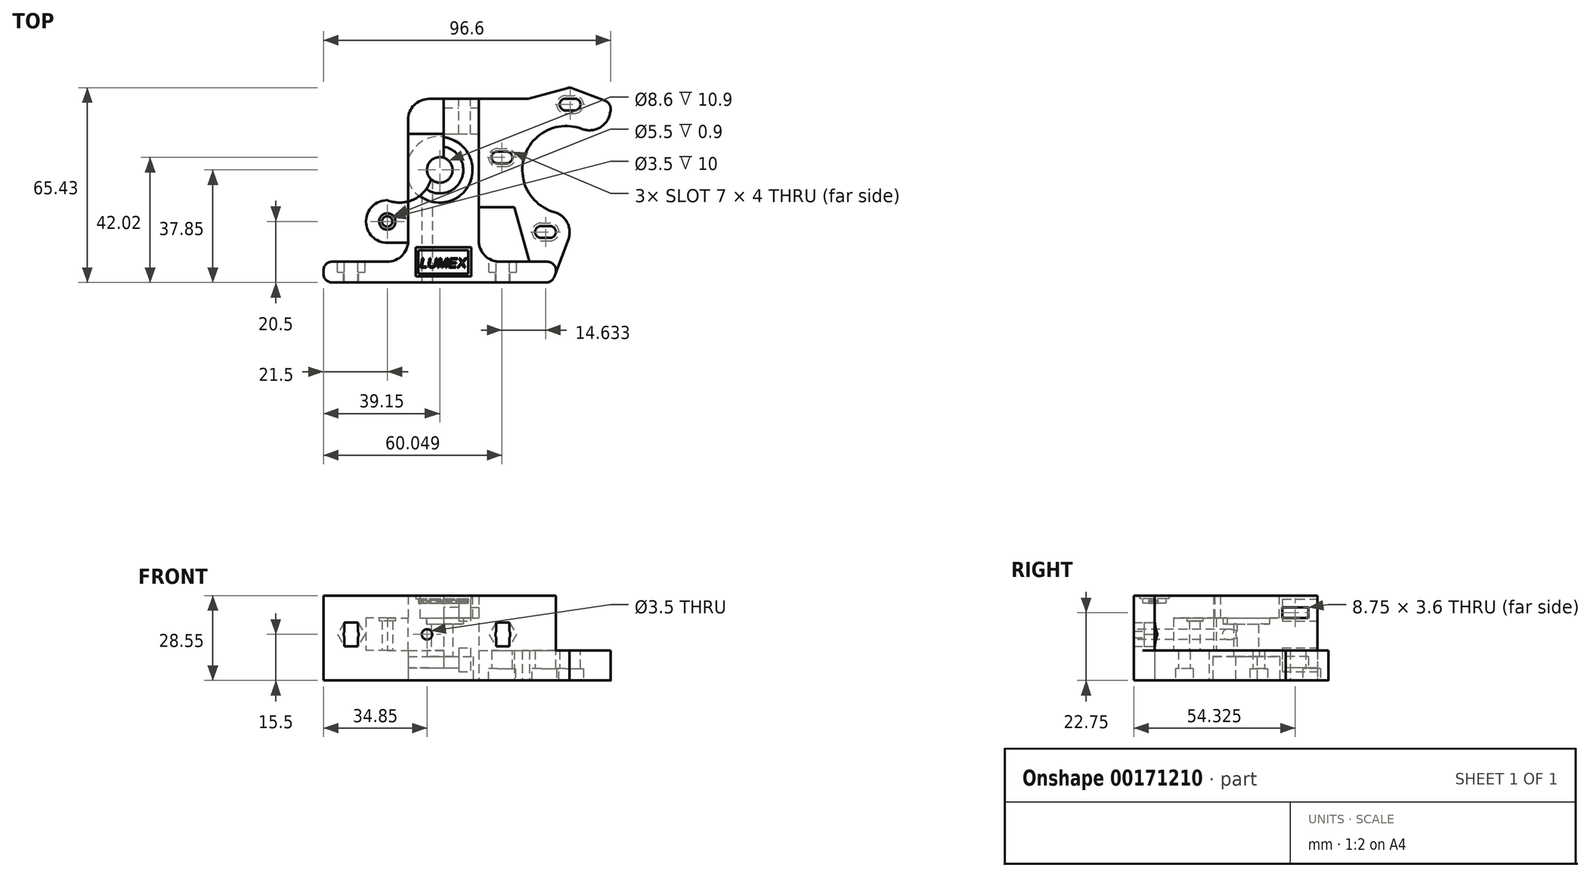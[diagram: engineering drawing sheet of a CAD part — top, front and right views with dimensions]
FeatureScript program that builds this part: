
annotation { "Feature Type Name" : "Feature", "Feature Type Description" : "" }
export const myFeature = defineFeature(function(context is Context, id is Id, definition is map)
    precondition{}
    {
        {
            var Q0;
            Q0=qCreatedBy(makeId("Top.planeOp"),FACE);
            var sketch = newSketch(context, id + "F0", { "sketchPlane" : qUnion([Q0])});
            skCircle(sketch, "E0", {"center": v(0, 0) * mm, "radius": 11.25 * mm});
            skCircle(sketch, "E1", {"center": v(42.5, 0) * mm, "radius": 14.75 * mm});
            skLineSegment(sketch, "E2", {"start": v(-10.65, 23.85) * mm, "end": v(-10.65, -30.85) * mm});
            skLineSegment(sketch, "E3", {"start": v(-10.65, -30.85) * mm, "end": v(-39.15, -30.85) * mm});
            skLineSegment(sketch, "E4", {"start": v(-39.15, -30.85) * mm, "end": v(-39.15, -37.85) * mm});
            skLineSegment(sketch, "E5", {"start": v(-39.15, -37.85) * mm, "end": v(37.75, -37.85) * mm});
            skLineSegment(sketch, "E6", {"start": v(-10.65, 23.85) * mm, "end": v(29.35, 23.85) * mm});
            skLineSegment(sketch, "E7", {"start": v(37.75, -37.85) * mm, "end": v(46.67, -14.15) * mm});
            skLineSegment(sketch, "E8", {"start": v(29.35, 23.85) * mm, "end": v(43.84, 27.73) * mm});
            skLineSegment(sketch, "E9", {"start": v(43.84, 27.73) * mm, "end": v(57.85, 22.35) * mm});
            skLineSegment(sketch, "E10", {"start": v(57.85, 22.35) * mm, "end": v(55.15, 7.6) * mm});
            skLineSegment(sketch, "E11", {"start": v(-10.65, -30.85) * mm, "end": v(40.38, -30.85) * mm});
            skLineSegment(sketch, "E12", {"start": v(13.1, 23.85) * mm, "end": v(13.1, -30.85) * mm});
            skLineSegment(sketch, "E13", {"start": v(13.1, -12.56) * mm, "end": v(25.1, -12.56) * mm});
            skLineSegment(sketch, "E14.bottom", {"start": v(40.3, 23.96) * mm, "end": v(47.3, 23.96) * mm});
            skLineSegment(sketch, "E14.top", {"start": v(40.3, 19.96) * mm, "end": v(47.3, 19.96) * mm});
            skLineSegment(sketch, "E14.left", {"start": v(40.3, 23.96) * mm, "end": v(40.3, 19.96) * mm});
            skLineSegment(sketch, "E14.right", {"start": v(47.3, 23.96) * mm, "end": v(47.3, 19.96) * mm});
            skPoint(sketch, "E14.middle", {"position": v(43.8, 21.96) * mm});
            skLineSegment(sketch, "E15.bottom", {"start": v(17.4, 6.17) * mm, "end": v(24.4, 6.17) * mm});
            skLineSegment(sketch, "E15.top", {"start": v(17.4, 2.17) * mm, "end": v(24.4, 2.17) * mm});
            skLineSegment(sketch, "E15.left", {"start": v(17.4, 6.17) * mm, "end": v(17.4, 2.17) * mm});
            skLineSegment(sketch, "E15.right", {"start": v(24.4, 6.17) * mm, "end": v(24.4, 2.17) * mm});
            skPoint(sketch, "E15.middle", {"position": v(20.9, 4.17) * mm});
            skLineSegment(sketch, "E16.bottom", {"start": v(32.03, -18.87) * mm, "end": v(39.03, -18.87) * mm});
            skLineSegment(sketch, "E16.top", {"start": v(32.03, -22.87) * mm, "end": v(39.03, -22.87) * mm});
            skLineSegment(sketch, "E16.left", {"start": v(32.03, -18.87) * mm, "end": v(32.03, -22.87) * mm});
            skLineSegment(sketch, "E16.right", {"start": v(39.03, -18.87) * mm, "end": v(39.03, -22.87) * mm});
            skPoint(sketch, "E16.middle", {"position": v(35.53, -20.87) * mm});
            skLineSegment(sketch, "E17.bottom", {"start": v(16.4, 7.17) * mm, "end": v(25.4, 7.17) * mm});
            skLineSegment(sketch, "E17.top", {"start": v(16.4, 1.17) * mm, "end": v(25.4, 1.17) * mm});
            skLineSegment(sketch, "E17.left", {"start": v(16.4, 7.17) * mm, "end": v(16.4, 1.17) * mm});
            skLineSegment(sketch, "E17.right", {"start": v(25.4, 7.17) * mm, "end": v(25.4, 1.17) * mm});
            skLineSegment(sketch, "E18.bottom", {"start": v(31.03, -17.87) * mm, "end": v(40.03, -17.87) * mm});
            skLineSegment(sketch, "E18.top", {"start": v(31.03, -23.87) * mm, "end": v(40.03, -23.87) * mm});
            skLineSegment(sketch, "E18.left", {"start": v(31.03, -17.87) * mm, "end": v(31.03, -23.87) * mm});
            skLineSegment(sketch, "E18.right", {"start": v(40.03, -17.87) * mm, "end": v(40.03, -23.87) * mm});
            skLineSegment(sketch, "E19.bottom", {"start": v(39.3, 24.96) * mm, "end": v(48.3, 24.96) * mm});
            skLineSegment(sketch, "E19.top", {"start": v(39.3, 18.96) * mm, "end": v(48.3, 18.96) * mm});
            skLineSegment(sketch, "E19.left", {"start": v(39.3, 24.96) * mm, "end": v(39.3, 18.96) * mm});
            skLineSegment(sketch, "E19.right", {"start": v(48.3, 24.96) * mm, "end": v(48.3, 18.96) * mm});
            skLineSegment(sketch, "E20", {"start": v(25.1, -12.56) * mm, "end": v(30.1, -30.85) * mm});
            skLineSegment(sketch, "E21", {"start": v(-10.65, 12.1) * mm, "end": v(1.35, 12.1) * mm});
            skLineSegment(sketch, "E22", {"start": v(1.35, 12.1) * mm, "end": v(1.35, 23.85) * mm});
            skLineSegment(sketch, "E23", {"start": v(1.35, 20.85) * mm, "end": v(6.35, 20.85) * mm});
            skLineSegment(sketch, "E24", {"start": v(6.35, 20.85) * mm, "end": v(6.35, 23.85) * mm});
            skLineSegment(sketch, "E25", {"start": v(1.35, 12.1) * mm, "end": v(10.35, 12.1) * mm});
            skLineSegment(sketch, "E26", {"start": v(10.35, 12.1) * mm, "end": v(10.35, 23.85) * mm});
            skLineSegment(sketch, "E27", {"start": v(6.35, 20.85) * mm, "end": v(6.35, 12.1) * mm});
            skCircle(sketch, "E28", {"center": v(0, 0) * mm, "radius": 4.3 * mm});
            skSolve(sketch);
        }
        {
            var Q0;
            {var subQ11=sQuery(id+"F0.wireOp",EDGE,"E8");Q0=makeQuery(id+"F0.imprint","IMPRINT",FACE,{"disambiguationData":[TD([[makeQuery(id+"F0.imprint","IMPRINT",EDGE,{"derivedFrom":subQ11}),-1.0]])]});}
            var Q1;
            {var subQ3=sQuery(id+"F0.wireOp",EDGE,"E21");Q1=makeQuery(id+"F0.imprint","IMPRINT",FACE,{"disambiguationData":[TD([[makeQuery(id+"F0.imprint","IMPRINT",EDGE,{"derivedFrom":subQ3}),-1.0]])]});}
            var Q2;
            {var subQ6=sQuery(id+"F0.wireOp",EDGE,"E3");Q2=makeQuery(id+"F0.imprint","IMPRINT",FACE,{"disambiguationData":[TD([[makeQuery(id+"F0.imprint","IMPRINT",EDGE,{"derivedFrom":subQ6}),1.0]])]});}
            var Q3;
            {var subQ4=sQuery(id+"F0.wireOp",EDGE,"E23");Q3=makeQuery(id+"F0.imprint","IMPRINT",FACE,{"disambiguationData":[TD([[makeQuery(id+"F0.imprint","IMPRINT",EDGE,{"derivedFrom":subQ4}),1.0]])]});}
            extrude(context, id + "F1", {"entities" : qUnion([Q0, Q1, Q2, Q3]), "depth" : 10.05 * mm});
        }
        {
            var Q0;
            Q0=makeQuery(id+"F0.imprint","IMPRINT",FACE,{"disambiguationData":[TD([[makeQuery(id+"F0.imprint","IMPRINT",EDGE,{"derivedFrom":sQuery(id+"F0.wireOp",EDGE,"E15.bottom")}),1.0]])]});
            var Q1;
            Q1=makeQuery(id+"F0.imprint","IMPRINT",FACE,{"disambiguationData":[TD([[makeQuery(id+"F0.imprint","IMPRINT",EDGE,{"derivedFrom":sQuery(id+"F0.wireOp",EDGE,"E14.bottom")}),1.0]])]});
            var Q2;
            Q2=makeQuery(id+"F0.imprint","IMPRINT",FACE,{"disambiguationData":[TD([[makeQuery(id+"F0.imprint","IMPRINT",EDGE,{"derivedFrom":sQuery(id+"F0.wireOp",EDGE,"E16.bottom")}),1.0]])]});
            extrude(context, id + "F2", {"entities" : qUnion([Q0, Q1, Q2]), "operationType" : NewBodyOperationType.ADD, "depth" : 10.05 * mm, "hasSecondDirection" : true, "secondDirectionOppositeDirection" : false, "secondDirectionDepth" : 4 * mm});
        }
        {
            var Q0;
            {var subQ3=sQuery(id+"F0.wireOp",EDGE,"E23");Q0=makeQuery(id+"F0.imprint","IMPRINT",FACE,{"disambiguationData":[TD([[makeQuery(id+"F0.imprint","IMPRINT",EDGE,{"derivedFrom":subQ3}),-1.0]])]});}
            var Q1;
            {var subQ1=sQuery(id+"F0.wireOp",EDGE,"E21");Q1=makeQuery(id+"F0.imprint","IMPRINT",FACE,{"disambiguationData":[TD([[makeQuery(id+"F0.imprint","IMPRINT",EDGE,{"derivedFrom":subQ1}),1.0]])]});}
            extrude(context, id + "F3", {"entities" : qUnion([Q0, Q1]), "operationType" : NewBodyOperationType.ADD, "depth" : 4.25 * mm});
        }
        {
            var Q0;
            {var subQ0=sQuery(id+"F0.wireOp",EDGE,"E24");Q0=makeQuery(id+"F0.imprint","IMPRINT",FACE,{"disambiguationData":[TD([[makeQuery(id+"F0.imprint","IMPRINT",EDGE,{"derivedFrom":subQ0}),-1.0]])]});}
            extrude(context, id + "F4", {"entities" : qUnion([Q0]), "operationType" : NewBodyOperationType.ADD, "depth" : 3 * mm});
        }
        {
            var Q0;
            Q0=makeQuery(id+"F0.imprint","IMPRINT",FACE,{"disambiguationData":[TD([[makeQuery(id+"F0.imprint","IMPRINT",EDGE,{"derivedFrom":sQuery(id+"F0.wireOp",EDGE,"E28")}),-1.0]])]});
            var Q1;
            {var subQ3=sQuery(id+"F0.wireOp",EDGE,"E23");Q1=makeQuery(id+"F0.imprint","IMPRINT",FACE,{"disambiguationData":[TD([[makeQuery(id+"F0.imprint","IMPRINT",EDGE,{"derivedFrom":subQ3}),-1.0]])]});}
            extrude(context, id + "F5", {"entities" : qUnion([Q0, Q1]), "operationType" : NewBodyOperationType.ADD, "depth" : 10.05 * mm, "hasSecondDirection" : true, "secondDirectionOppositeDirection" : false, "secondDirectionDepth" : 8.05 * mm});
        }
        {
            var Q0;
            {var subQ0=sQuery(id+"F0.wireOp",EDGE,"E25");var subQ1=sQuery(id+"F0.wireOp",EDGE,"E23");var subQ2=sQuery(id+"F0.wireOp",EDGE,"E22");var subQ3=sQuery(id+"F0.wireOp",EDGE,"E2");var subQ4=sQuery(id+"F0.wireOp",EDGE,"E0");var subQ5=sQuery(id+"F0.wireOp",EDGE,"E18.right");var subQ6=sQuery(id+"F0.wireOp",EDGE,"E18.left");var subQ7=sQuery(id+"F0.wireOp",EDGE,"E18.top");var subQ8=sQuery(id+"F0.wireOp",EDGE,"E18.bottom");var subQ9=sQuery(id+"F0.wireOp",EDGE,"E17.right");var subQ10=sQuery(id+"F0.wireOp",EDGE,"E17.left");var subQ11=sQuery(id+"F0.wireOp",EDGE,"E17.top");var subQ12=sQuery(id+"F0.wireOp",EDGE,"E17.bottom");var subQ13=sQuery(id+"F0.wireOp",EDGE,"E19.right");var subQ14=sQuery(id+"F0.wireOp",EDGE,"E19.left");var subQ15=sQuery(id+"F0.wireOp",EDGE,"E19.top");var subQ16=sQuery(id+"F0.wireOp",EDGE,"E19.bottom");var subQ17=sQuery(id+"F0.wireOp",EDGE,"E6");Q0=makeQuery(id+"F5.boolean.opBoolean","MERGE",FACE,{"derivedFrom":[makeQuery(id+"F1.opExtrude","CAP_FACE",FACE,{"disambiguationData":[OSD([subQ17,subQ2,subQ1,sQuery(id+"F0.wireOp",EDGE,"E24")])],"isStart":false}),makeQuery(id+"F2.boolean.opBoolean","MERGE",FACE,{"derivedFrom":[makeQuery(id+"F1.opExtrude","CAP_FACE",FACE,{"disambiguationData":[OSD([subQ4,sQuery(id+"F0.wireOp",EDGE,"E1"),subQ3,sQuery(id+"F0.wireOp",EDGE,"E3"),sQuery(id+"F0.wireOp",EDGE,"E4"),sQuery(id+"F0.wireOp",EDGE,"E5"),subQ17,sQuery(id+"F0.wireOp",EDGE,"E7"),sQuery(id+"F0.wireOp",EDGE,"E8"),sQuery(id+"F0.wireOp",EDGE,"E9"),sQuery(id+"F0.wireOp",EDGE,"E10"),sQuery(id+"F0.wireOp",EDGE,"E11"),sQuery(id+"F0.wireOp",EDGE,"E12"),sQuery(id+"F0.wireOp",EDGE,"E13"),subQ12,subQ11,subQ10,subQ9,subQ8,subQ7,subQ6,subQ5,subQ16,subQ15,subQ14,subQ13,sQuery(id+"F0.wireOp",EDGE,"E20"),sQuery(id+"F0.wireOp",EDGE,"E21"),subQ0,sQuery(id+"F0.wireOp",EDGE,"E26")])],"isStart":false}),makeQuery(id+"F2.opExtrude","CAP_FACE",FACE,{"disambiguationData":[OSD([sQuery(id+"F0.wireOp",EDGE,"E14.bottom"),sQuery(id+"F0.wireOp",EDGE,"E14.top"),sQuery(id+"F0.wireOp",EDGE,"E14.left"),sQuery(id+"F0.wireOp",EDGE,"E14.right"),subQ16,subQ15,subQ14,subQ13])],"isStart":false}),makeQuery(id+"F2.opExtrude","CAP_FACE",FACE,{"disambiguationData":[OSD([sQuery(id+"F0.wireOp",EDGE,"E15.bottom"),sQuery(id+"F0.wireOp",EDGE,"E15.top"),sQuery(id+"F0.wireOp",EDGE,"E15.left"),sQuery(id+"F0.wireOp",EDGE,"E15.right"),subQ12,subQ11,subQ10,subQ9])],"isStart":false}),makeQuery(id+"F2.opExtrude","CAP_FACE",FACE,{"disambiguationData":[OSD([sQuery(id+"F0.wireOp",EDGE,"E16.bottom"),sQuery(id+"F0.wireOp",EDGE,"E16.top"),sQuery(id+"F0.wireOp",EDGE,"E16.left"),sQuery(id+"F0.wireOp",EDGE,"E16.right"),subQ8,subQ7,subQ6,subQ5])],"isStart":false})]}),makeQuery(id+"F5.opExtrude","CAP_FACE",FACE,{"disambiguationData":[OSD([subQ4,subQ3,sQuery(id+"F0.wireOp",EDGE,"E28")])],"isStart":false}),makeQuery(id+"F5.opExtrude","CAP_FACE",FACE,{"disambiguationData":[OSD([subQ2,subQ1,subQ0,sQuery(id+"F0.wireOp",EDGE,"E27")])],"isStart":false})]});}
            var sketch = newSketch(context, id + "F6", { "sketchPlane" : qUnion([Q0])});
            skLineSegment(sketch, "E29", {"start": v(13.1, -30.85) * mm, "end": v(13.1, 23.85) * mm});
            skLineSegment(sketch, "E30", {"start": v(13.1, -30.85) * mm, "end": v(13.1, -37.85) * mm});
            skLineSegment(sketch, "E31", {"start": v(-10.65, -30.85) * mm, "end": v(-10.65, -37.85) * mm});
            skLineSegment(sketch, "E32", {"start": v(-10.65, -30.85) * mm, "end": v(-10.65, 23.85) * mm});
            skLineSegment(sketch, "E33", {"start": v(-10.65, 23.85) * mm, "end": v(13.1, 23.85) * mm});
            skCircle(sketch, "E34", {"center": v(0, 0) * mm, "radius": 4.3 * mm});
            skCircle(sketch, "E35", {"center": v(0, 0) * mm, "radius": 7.9 * mm});
            skCircle(sketch, "E36", {"center": v(0, 0) * mm, "radius": 11 * mm});
            skLineSegment(sketch, "E37", {"start": v(1.35, 23.85) * mm, "end": v(1.35, 4.08) * mm});
            skLineSegment(sketch, "E38", {"start": v(13.1, -30.85) * mm, "end": v(40.38, -30.85) * mm});
            skLineSegment(sketch, "E39", {"start": v(40.38, -30.85) * mm, "end": v(37.75, -37.85) * mm});
            skLineSegment(sketch, "E40", {"start": v(37.75, -37.85) * mm, "end": v(13.1, -37.85) * mm});
            skLineSegment(sketch, "E41", {"start": v(-10.65, -30.85) * mm, "end": v(-39.15, -30.85) * mm});
            skLineSegment(sketch, "E42", {"start": v(-39.15, -30.85) * mm, "end": v(-39.15, -37.85) * mm});
            skLineSegment(sketch, "E43", {"start": v(-39.15, -37.85) * mm, "end": v(-10.65, -37.85) * mm});
            skCircle(sketch, "E44", {"center": v(-13.5, 0) * mm, "radius": 11 * mm});
            skCircle(sketch, "E45", {"center": v(-17.65, -17.35) * mm, "radius": 1.75 * mm});
            skArc(sketch, "E46", {"start": v(-17.65, -10.19) * mm, "mid": v(-24.81, -17.35) * mm, "end": v(-17.65, -24.51) * mm});
            skLineSegment(sketch, "E47", {"start": v(-17.65, -24.51) * mm, "end": v(-10.65, -24.51) * mm});
            skCircle(sketch, "E48", {"center": v(-17.65, -17.35) * mm, "radius": 2.75 * mm});
            skLineSegment(sketch, "E49", {"start": v(6.35, 23.85) * mm, "end": v(6.35, 12.1) * mm});
            skLineSegment(sketch, "E50", {"start": v(6.35, 12.1) * mm, "end": v(10.35, 12.1) * mm});
            skLineSegment(sketch, "E51", {"start": v(10.35, 12.1) * mm, "end": v(10.35, 23.85) * mm});
            skLineSegment(sketch, "E52", {"start": v(10.35, 23.85) * mm, "end": v(6.35, 23.85) * mm});
            skLineSegment(sketch, "E53", {"start": v(35.02, -30.85) * mm, "end": v(35.02, -37.85) * mm});
            skSolve(sketch);
        }
        {
            var Q0;
            {var subQ0=sQuery(id+"F6.wireOp",EDGE,"E37");var subQ1=sQuery(id+"F6.wireOp",EDGE,"E35");var subQ2=makeQuery(id+"F6.imprint","INTERSECT",VERTEX,{"derivedFrom":[subQ1,subQ0]});Q0=makeQuery(id+"F6.imprint","IMPRINT",FACE,{"disambiguationData":[TD([[makeQuery(id+"F6.imprint","IMPRINT",EDGE,{"disambiguationData":[TD([[subQ2,1.0]])],"derivedFrom":subQ1}),-1.0]])]});}
            var Q1;
            {var subQ1=sQuery(id+"F6.wireOp",EDGE,"E46");Q1=makeQuery(id+"F6.imprint","IMPRINT",FACE,{"disambiguationData":[TD([[makeQuery(id+"F6.imprint","IMPRINT",EDGE,{"derivedFrom":subQ1}),1.0]])]});}
            var Q2;
            {var subQ9=sQuery(id+"F6.wireOp",EDGE,"E30");Q2=makeQuery(id+"F6.imprint","IMPRINT",FACE,{"disambiguationData":[TD([[makeQuery(id+"F6.imprint","IMPRINT",EDGE,{"derivedFrom":subQ9}),-1.0]])]});}
            var Q3;
            {var subQ0=sQuery(id+"F6.wireOp",EDGE,"E39");Q3=makeQuery(id+"F6.imprint","IMPRINT",FACE,{"disambiguationData":[TD([[makeQuery(id+"F6.imprint","IMPRINT",EDGE,{"derivedFrom":subQ0}),1.0]])]});}
            extrude(context, id + "F7", {"entities" : qUnion([Q0, Q1, Q2, Q3]), "operationType" : NewBodyOperationType.ADD, "depth" : 10.9 * mm});
        }
        {
            var Q0;
            {var subQ0=sQuery(id+"F6.wireOp",EDGE,"E37");var subQ1=sQuery(id+"F6.wireOp",EDGE,"E34");var subQ2=makeQuery(id+"F6.imprint","INTERSECT",VERTEX,{"derivedFrom":[subQ1,subQ0]});Q0=makeQuery(id+"F6.imprint","IMPRINT",FACE,{"disambiguationData":[TD([[makeQuery(id+"F6.imprint","IMPRINT",EDGE,{"disambiguationData":[TD([[subQ2,1.0]])],"derivedFrom":subQ1}),-1.0]])]});}
            extrude(context, id + "F8", {"entities" : qUnion([Q0]), "operationType" : NewBodyOperationType.ADD, "depth" : 8.9 * mm});
        }
        {
            var Q0;
            Q0=makeQuery(id+"F6.imprint","IMPRINT",FACE,{"disambiguationData":[TD([[makeQuery(id+"F6.imprint","IMPRINT",EDGE,{"derivedFrom":sQuery(id+"F6.wireOp",EDGE,"E49")}),-1.0]])]});
            extrude(context, id + "F9", {"entities" : qUnion([Q0]), "operationType" : NewBodyOperationType.ADD, "depth" : 10 * mm, "hasSecondDirection" : true, "secondDirectionOppositeDirection" : false, "secondDirectionDepth" : .9 * mm});
        }
        {
            var Q0;
            Q0=makeQuery(id+"F6.imprint","IMPRINT",FACE,{"disambiguationData":[TD([[makeQuery(id+"F6.imprint","IMPRINT",EDGE,{"derivedFrom":sQuery(id+"F6.wireOp",EDGE,"E31")}),-1.0]])]});
            var Q1;
            {var subQ3=sQuery(id+"F6.wireOp",EDGE,"E30");Q1=makeQuery(id+"F6.imprint","IMPRINT",FACE,{"disambiguationData":[TD([[makeQuery(id+"F6.imprint","IMPRINT",EDGE,{"derivedFrom":subQ3}),1.0]])]});}
            extrude(context, id + "F10", {"entities" : qUnion([Q0, Q1]), "operationType" : NewBodyOperationType.ADD, "depth" : 1.45 * mm});
        }
        {
            var Q0;
            Q0=makeQuery(id+"F6.imprint","IMPRINT",FACE,{"disambiguationData":[TD([[makeQuery(id+"F6.imprint","IMPRINT",EDGE,{"derivedFrom":sQuery(id+"F6.wireOp",EDGE,"E31")}),-1.0]])]});
            var Q1;
            {var subQ3=sQuery(id+"F6.wireOp",EDGE,"E30");Q1=makeQuery(id+"F6.imprint","IMPRINT",FACE,{"disambiguationData":[TD([[makeQuery(id+"F6.imprint","IMPRINT",EDGE,{"derivedFrom":subQ3}),1.0]])]});}
            extrude(context, id + "F11", {"entities" : qUnion([Q0, Q1]), "operationType" : NewBodyOperationType.ADD, "depth" : 10.9 * mm, "hasSecondDirection" : true, "secondDirectionOppositeDirection" : false, "secondDirectionDepth" : 9.45 * mm});
        }
        {
            var Q0;
            Q0=makeQuery(id+"F11.opExtrude","SWEPT_FACE",FACE,{"disambiguationData":[OSD([sQuery(id+"F6.wireOp",EDGE,"E38")])]});
            var sketch = newSketch(context, id + "F12", { "sketchPlane" : qUnion([Q0])});
            skLineSegment(sketch, "E54", {"start": v(-35.02, 19.5) * mm, "end": v(-13.1, 19.5) * mm});
            skLineSegment(sketch, "E55", {"start": v(-35.02, 19.5) * mm, "end": v(-35.02, 11.5) * mm});
            skLineSegment(sketch, "E56", {"start": v(-13.1, 19.5) * mm, "end": v(-13.1, 11.5) * mm});
            skLineSegment(sketch, "E57", {"start": v(-35.02, 11.5) * mm, "end": v(-13.1, 11.5) * mm});
            skLineSegment(sketch, "E58.bottom", {"start": v(-23.45, 19.5) * mm, "end": v(-18.95, 19.5) * mm});
            skLineSegment(sketch, "E58.top", {"start": v(-23.45, 11.5) * mm, "end": v(-18.95, 11.5) * mm});
            skLineSegment(sketch, "E58.left", {"start": v(-23.45, 19.5) * mm, "end": v(-23.45, 11.5) * mm});
            skLineSegment(sketch, "E58.right", {"start": v(-18.95, 19.5) * mm, "end": v(-18.95, 11.5) * mm});
            skLineSegment(sketch, "E59", {"start": v(-23.45, 19.5) * mm, "end": v(-25.82, 15.5) * mm});
            skLineSegment(sketch, "E60", {"start": v(-25.82, 15.5) * mm, "end": v(-23.45, 11.5) * mm});
            skLineSegment(sketch, "E61", {"start": v(-18.95, 19.5) * mm, "end": v(-16.57, 15.5) * mm});
            skLineSegment(sketch, "E62", {"start": v(-16.57, 15.5) * mm, "end": v(-18.95, 11.5) * mm});
            skLineSegment(sketch, "E63", {"start": v(-25.82, 15.5) * mm, "end": v(-23.45, 15.5) * mm});
            skLineSegment(sketch, "E64", {"start": v(-16.57, 15.5) * mm, "end": v(-18.95, 15.5) * mm});
            skCircle(sketch, "E65", {"center": v(-21.2, 15.5) * mm, "radius": 2.5 * mm});
            skLineSegment(sketch, "E66", {"start": v(-13.1, 11.5) * mm, "end": v(39.15, 11.5) * mm});
            skLineSegment(sketch, "E67", {"start": v(-13.1, 19.5) * mm, "end": v(39.15, 19.5) * mm});
            skLineSegment(sketch, "E68", {"start": v(39.15, 19.5) * mm, "end": v(39.15, 11.5) * mm});
            skCircle(sketch, "E69", {"center": v(29.8, 15.5) * mm, "radius": 2.5 * mm});
            skLineSegment(sketch, "E70", {"start": v(32.05, 19.5) * mm, "end": v(32.05, 11.5) * mm});
            skLineSegment(sketch, "E71", {"start": v(27.55, 19.5) * mm, "end": v(27.55, 11.5) * mm});
            skLineSegment(sketch, "E72", {"start": v(27.55, 19.5) * mm, "end": v(25.17, 15.5) * mm});
            skLineSegment(sketch, "E73", {"start": v(25.17, 15.5) * mm, "end": v(27.55, 11.5) * mm});
            skLineSegment(sketch, "E74", {"start": v(32.05, 19.5) * mm, "end": v(34.42, 15.5) * mm});
            skLineSegment(sketch, "E75", {"start": v(34.42, 15.5) * mm, "end": v(32.05, 11.5) * mm});
            skLineSegment(sketch, "E76", {"start": v(34.42, 15.5) * mm, "end": v(32.05, 15.5) * mm});
            skLineSegment(sketch, "E77", {"start": v(25.18, 15.5) * mm, "end": v(27.55, 15.5) * mm});
            skSolve(sketch);
        }
        {
            var Q0;
            {var subQ0=sQuery(id+"F12.wireOp",EDGE,"E59");Q0=makeQuery(id+"F12.imprint","IMPRINT",FACE,{"disambiguationData":[TD([[makeQuery(id+"F12.imprint","IMPRINT",EDGE,{"derivedFrom":subQ0}),1.0]])]});}
            var Q1;
            {var subQ0=sQuery(id+"F12.wireOp",EDGE,"E60");Q1=makeQuery(id+"F12.imprint","IMPRINT",FACE,{"disambiguationData":[TD([[makeQuery(id+"F12.imprint","IMPRINT",EDGE,{"derivedFrom":subQ0}),1.0]])]});}
            var Q2;
            {var subQ0=sQuery(id+"F12.wireOp",EDGE,"E62");Q2=makeQuery(id+"F12.imprint","IMPRINT",FACE,{"disambiguationData":[TD([[makeQuery(id+"F12.imprint","IMPRINT",EDGE,{"derivedFrom":subQ0}),-1.0]])]});}
            var Q3;
            {var subQ0=sQuery(id+"F12.wireOp",EDGE,"E61");Q3=makeQuery(id+"F12.imprint","IMPRINT",FACE,{"disambiguationData":[TD([[makeQuery(id+"F12.imprint","IMPRINT",EDGE,{"derivedFrom":subQ0}),-1.0]])]});}
            var Q4;
            {var subQ0=sQuery(id+"F12.wireOp",EDGE,"E58.bottom");Q4=makeQuery(id+"F12.imprint","IMPRINT",FACE,{"disambiguationData":[TD([[makeQuery(id+"F12.imprint","IMPRINT",EDGE,{"derivedFrom":subQ0}),1.0]])]});}
            var Q5;
            {var subQ5=sQuery(id+"F12.wireOp",EDGE,"E75");Q5=makeQuery(id+"F12.imprint","IMPRINT",FACE,{"disambiguationData":[TD([[makeQuery(id+"F12.imprint","IMPRINT",EDGE,{"derivedFrom":subQ5}),-1.0]])]});}
            var Q6;
            {var subQ3=sQuery(id+"F12.wireOp",EDGE,"E71");var subQ5=sQuery(id+"F12.wireOp",EDGE,"E69");var subQ6=makeQuery(id+"F12.imprint","INTERSECT",VERTEX,{"disambiguationData":[OD(1.0)],"derivedFrom":[subQ5,subQ3]});Q6=makeQuery(id+"F12.imprint","IMPRINT",FACE,{"disambiguationData":[TD([[makeQuery(id+"F12.imprint","IMPRINT",EDGE,{"disambiguationData":[TD([[subQ6,-1.0]])],"derivedFrom":subQ5}),-1.0]])]});}
            var Q7;
            {var subQ5=sQuery(id+"F12.wireOp",EDGE,"E73");Q7=makeQuery(id+"F12.imprint","IMPRINT",FACE,{"disambiguationData":[TD([[makeQuery(id+"F12.imprint","IMPRINT",EDGE,{"derivedFrom":subQ5}),1.0]])]});}
            var Q8;
            {var subQ0=sQuery(id+"F12.wireOp",EDGE,"E70");var subQ5=sQuery(id+"F12.wireOp",EDGE,"E69");var subQ6=makeQuery(id+"F12.imprint","INTERSECT",VERTEX,{"disambiguationData":[OD(0.0)],"derivedFrom":[subQ5,subQ0]});Q8=makeQuery(id+"F12.imprint","IMPRINT",FACE,{"disambiguationData":[TD([[makeQuery(id+"F12.imprint","IMPRINT",EDGE,{"disambiguationData":[TD([[subQ6,-1.0]])],"derivedFrom":subQ5}),-1.0]])]});}
            var Q9;
            {var subQ5=sQuery(id+"F12.wireOp",EDGE,"E72");Q9=makeQuery(id+"F12.imprint","IMPRINT",FACE,{"disambiguationData":[TD([[makeQuery(id+"F12.imprint","IMPRINT",EDGE,{"derivedFrom":subQ5}),1.0]])]});}
            var Q10;
            {var subQ5=sQuery(id+"F12.wireOp",EDGE,"E74");Q10=makeQuery(id+"F12.imprint","IMPRINT",FACE,{"disambiguationData":[TD([[makeQuery(id+"F12.imprint","IMPRINT",EDGE,{"derivedFrom":subQ5}),-1.0]])]});}
            var Q11;
            {var subQ0=sQuery(id+"F12.wireOp",EDGE,"E58.top");Q11=makeQuery(id+"F12.imprint","IMPRINT",FACE,{"disambiguationData":[TD([[makeQuery(id+"F12.imprint","IMPRINT",EDGE,{"derivedFrom":subQ0}),-1.0]])]});}
            extrude(context, id + "F13", {"entities" : qUnion([Q0, Q1, Q2, Q3, Q4, Q5, Q6, Q7, Q8, Q9, Q10, Q11]), "operationType" : NewBodyOperationType.ADD, "oppositeDirection" : true, "depth" : 7 * mm, "hasSecondDirection" : true, "secondDirectionOppositeDirection" : true, "secondDirectionDepth" : 3.5 * mm});
        }
        {
            var Q0;
            {var subQ0=sQuery(id+"F12.wireOp",EDGE,"E56");Q0=makeQuery(id+"F12.imprint","IMPRINT",FACE,{"disambiguationData":[TD([[makeQuery(id+"F12.imprint","IMPRINT",EDGE,{"derivedFrom":subQ0}),-1.0]])]});}
            var Q1;
            {var subQ1=sQuery(id+"F12.wireOp",EDGE,"E68");Q1=makeQuery(id+"F12.imprint","IMPRINT",FACE,{"disambiguationData":[TD([[makeQuery(id+"F12.imprint","IMPRINT",EDGE,{"derivedFrom":subQ1}),-1.0]])]});}
            var Q2;
            {var subQ1=sQuery(id+"F12.wireOp",EDGE,"E56");Q2=makeQuery(id+"F12.imprint","IMPRINT",FACE,{"disambiguationData":[TD([[makeQuery(id+"F12.imprint","IMPRINT",EDGE,{"derivedFrom":subQ1}),1.0]])]});}
            var Q3;
            {var subQ2=sQuery(id+"F12.wireOp",EDGE,"E55");Q3=makeQuery(id+"F12.imprint","IMPRINT",FACE,{"disambiguationData":[TD([[makeQuery(id+"F12.imprint","IMPRINT",EDGE,{"derivedFrom":subQ2}),1.0]])]});}
            extrude(context, id + "F14", {"entities" : qUnion([Q0, Q1, Q2, Q3]), "operationType" : NewBodyOperationType.ADD, "oppositeDirection" : true, "depth" : 7 * mm});
        }
        {
            var Q0;
            {var subQ0=sQuery(id+"F6.wireOp",EDGE,"E31");var subQ1=sQuery(id+"F6.wireOp",EDGE,"E53");var subQ2=sQuery(id+"F6.wireOp",EDGE,"E40");var subQ3=sQuery(id+"F6.wireOp",EDGE,"E38");var subQ4=sQuery(id+"F6.wireOp",EDGE,"E30");Q0=makeQuery(id+"F11.boolean.opBoolean","MERGE",FACE,{"derivedFrom":[makeQuery(id+"F7.opExtrude","CAP_FACE",FACE,{"disambiguationData":[OSD([sQuery(id+"F0.wireOp",EDGE,"E5"),sQuery(id+"F6.wireOp",EDGE,"E29"),subQ4,subQ0,sQuery(id+"F6.wireOp",EDGE,"E32"),sQuery(id+"F6.wireOp",EDGE,"E33"),sQuery(id+"F6.wireOp",EDGE,"E35"),sQuery(id+"F6.wireOp",EDGE,"E37"),sQuery(id+"F6.wireOp",EDGE,"E44"),sQuery(id+"F6.wireOp",EDGE,"E46"),sQuery(id+"F6.wireOp",EDGE,"E47"),sQuery(id+"F6.wireOp",EDGE,"E48"),sQuery(id+"F6.wireOp",EDGE,"E49"),sQuery(id+"F6.wireOp",EDGE,"E50"),sQuery(id+"F6.wireOp",EDGE,"E51")])],"isStart":false}),makeQuery(id+"F7.opExtrude","CAP_FACE",FACE,{"disambiguationData":[OSD([subQ3,sQuery(id+"F6.wireOp",EDGE,"E39"),subQ2,subQ1])],"isStart":false}),makeQuery(id+"F11.opExtrude","CAP_FACE",FACE,{"disambiguationData":[OSD([subQ4,subQ3,subQ2,subQ1])],"isStart":false}),makeQuery(id+"F11.opExtrude","CAP_FACE",FACE,{"disambiguationData":[OSD([subQ0,sQuery(id+"F6.wireOp",EDGE,"E41"),sQuery(id+"F6.wireOp",EDGE,"E42"),sQuery(id+"F6.wireOp",EDGE,"E43")])],"isStart":false})]});}
            var sketch = newSketch(context, id + "F15", { "sketchPlane" : qUnion([Q0])});
            skCircle(sketch, "E78", {"center": v(0, 0) * mm, "radius": 11 * mm});
            skLineSegment(sketch, "E79", {"start": v(1.35, 23.85) * mm, "end": v(1.35, 10.92) * mm});
            skLineSegment(sketch, "E80", {"start": v(1.35, 23.85) * mm, "end": v(6.35, 23.85) * mm});
            skLineSegment(sketch, "E81", {"start": v(6.35, 23.85) * mm, "end": v(6.35, 12.1) * mm});
            skLineSegment(sketch, "E82", {"start": v(6.35, 12.1) * mm, "end": v(10.35, 12.1) * mm});
            skLineSegment(sketch, "E83", {"start": v(10.35, 12.1) * mm, "end": v(10.35, 23.85) * mm});
            skLineSegment(sketch, "E84", {"start": v(10.35, 23.85) * mm, "end": v(13.1, 23.85) * mm});
            skLineSegment(sketch, "E85", {"start": v(13.1, 23.85) * mm, "end": v(13.1, -30.85) * mm});
            skLineSegment(sketch, "E86", {"start": v(13.1, -30.85) * mm, "end": v(40.38, -30.85) * mm});
            skLineSegment(sketch, "E87", {"start": v(40.38, -30.85) * mm, "end": v(37.75, -37.85) * mm});
            skLineSegment(sketch, "E88", {"start": v(37.75, -37.85) * mm, "end": v(-39.15, -37.85) * mm});
            skLineSegment(sketch, "E89", {"start": v(-39.15, -37.85) * mm, "end": v(-39.15, -30.85) * mm});
            skLineSegment(sketch, "E90", {"start": v(-39.15, -30.85) * mm, "end": v(-10.65, -30.85) * mm});
            skLineSegment(sketch, "E91", {"start": v(-10.65, -30.85) * mm, "end": v(-10.65, -2.75) * mm});
            skLineSegment(sketch, "E92", {"start": v(6.35, 12.1) * mm, "end": v(1.35, 12.1) * mm});
            skLineSegment(sketch, "E93", {"start": v(1.35, 20.85) * mm, "end": v(6.35, 20.85) * mm});
            skLineSegment(sketch, "E94", {"start": v(6.35, 23.85) * mm, "end": v(10.35, 23.85) * mm});
            skLineSegment(sketch, "E95", {"start": v(10.35, 20.85) * mm, "end": v(13.1, 20.85) * mm});
            skLineSegment(sketch, "E96", {"start": v(10.35, 12.1) * mm, "end": v(13.1, 12.1) * mm});
            skLineSegment(sketch, "E97.bottom", {"start": v(-8.15, -26) * mm, "end": v(10.6, -26) * mm});
            skLineSegment(sketch, "E97.top", {"start": v(-8.15, -35.85) * mm, "end": v(10.6, -35.85) * mm});
            skLineSegment(sketch, "E97.left", {"start": v(-8.15, -26) * mm, "end": v(-8.15, -35.85) * mm});
            skLineSegment(sketch, "E97.right", {"start": v(10.6, -26) * mm, "end": v(10.6, -35.85) * mm});
            skSolve(sketch);
        }
        {
            var Q0;
            Q0=makeQuery(id+"F15.imprint","IMPRINT",FACE,{"disambiguationData":[TD([[makeQuery(id+"F15.imprint","IMPRINT",EDGE,{"derivedFrom":sQuery(id+"F15.wireOp",EDGE,"E82")}),-1.0]])]});
            extrude(context, id + "F16", {"entities" : qUnion([Q0]), "operationType" : NewBodyOperationType.ADD, "depth" : 7.6 * mm});
        }
        {
            var Q0;
            {var subQ0=sQuery(id+"F15.wireOp",EDGE,"E80");Q0=makeQuery(id+"F15.imprint","IMPRINT",FACE,{"disambiguationData":[TD([[makeQuery(id+"F15.imprint","IMPRINT",EDGE,{"derivedFrom":subQ0}),-1.0]])]});}
            var Q1;
            {var subQ0=sQuery(id+"F15.wireOp",EDGE,"E84");Q1=makeQuery(id+"F15.imprint","IMPRINT",FACE,{"disambiguationData":[TD([[makeQuery(id+"F15.imprint","IMPRINT",EDGE,{"derivedFrom":subQ0}),-1.0]])]});}
            extrude(context, id + "F17", {"entities" : qUnion([Q0, Q1]), "operationType" : NewBodyOperationType.ADD, "depth" : 7.6 * mm});
        }
        {
            var Q0;
            {var subQ0=sQuery(id+"F15.wireOp",EDGE,"E92");Q0=makeQuery(id+"F15.imprint","IMPRINT",FACE,{"disambiguationData":[TD([[makeQuery(id+"F15.imprint","IMPRINT",EDGE,{"derivedFrom":subQ0}),-1.0]])]});}
            var Q1;
            {var subQ2=sQuery(id+"F15.wireOp",EDGE,"E95");Q1=makeQuery(id+"F15.imprint","IMPRINT",FACE,{"disambiguationData":[TD([[makeQuery(id+"F15.imprint","IMPRINT",EDGE,{"derivedFrom":subQ2}),-1.0]])]});}
            extrude(context, id + "F18", {"entities" : qUnion([Q0, Q1]), "operationType" : NewBodyOperationType.ADD, "depth" : 7.6 * mm, "hasSecondDirection" : true, "secondDirectionOppositeDirection" : false, "secondDirectionDepth" : 3.6 * mm});
        }
        {
            var Q0;
            {var subQ0=sQuery(id+"F15.wireOp",EDGE,"E82");Q0=makeQuery(id+"F15.imprint","IMPRINT",FACE,{"disambiguationData":[TD([[makeQuery(id+"F15.imprint","IMPRINT",EDGE,{"derivedFrom":subQ0}),1.0]])]});}
            extrude(context, id + "F19", {"entities" : qUnion([Q0]), "operationType" : NewBodyOperationType.ADD, "depth" : 7.6 * mm, "hasSecondDirection" : true, "secondDirectionOppositeDirection" : false, "secondDirectionDepth" : 6.4 * mm});
        }
        {
            var Q0;
            Q0=makeQuery(id+"F6.imprint","IMPRINT",FACE,{"disambiguationData":[TD([[makeQuery(id+"F6.imprint","IMPRINT",EDGE,{"derivedFrom":sQuery(id+"F6.wireOp",EDGE,"E45")}),-1.0]])]});
            extrude(context, id + "F20", {"entities" : qUnion([Q0]), "operationType" : NewBodyOperationType.ADD, "depth" : 10 * mm});
        }
        {
            var Q0;
            Q0=makeQuery(id+"F2.opExtrude","SWEPT_EDGE",EDGE,{"disambiguationData":[OSD([sQuery(id+"F0.wireOp",EDGE,"E15.bottom"),sQuery(id+"F0.wireOp",EDGE,"E15.right")])]});
            var Q1;
            Q1=makeQuery(id+"F2.opExtrude","SWEPT_EDGE",EDGE,{"disambiguationData":[OSD([sQuery(id+"F0.wireOp",EDGE,"E14.bottom"),sQuery(id+"F0.wireOp",EDGE,"E14.right")])]});
            var Q2;
            Q2=makeQuery(id+"F2.opExtrude","SWEPT_EDGE",EDGE,{"disambiguationData":[OSD([sQuery(id+"F0.wireOp",EDGE,"E16.bottom"),sQuery(id+"F0.wireOp",EDGE,"E16.right")])]});
            var Q3;
            Q3=makeQuery(id+"F2.opExtrude","SWEPT_EDGE",EDGE,{"disambiguationData":[OSD([sQuery(id+"F0.wireOp",EDGE,"E15.bottom"),sQuery(id+"F0.wireOp",EDGE,"E15.left")])]});
            var Q4;
            Q4=makeQuery(id+"F2.opExtrude","SWEPT_EDGE",EDGE,{"disambiguationData":[OSD([sQuery(id+"F0.wireOp",EDGE,"E14.bottom"),sQuery(id+"F0.wireOp",EDGE,"E14.left")])]});
            var Q5;
            Q5=makeQuery(id+"F2.opExtrude","SWEPT_EDGE",EDGE,{"disambiguationData":[OSD([sQuery(id+"F0.wireOp",EDGE,"E16.bottom"),sQuery(id+"F0.wireOp",EDGE,"E16.left")])]});
            var Q6;
            Q6=makeQuery(id+"F2.opExtrude","SWEPT_EDGE",EDGE,{"disambiguationData":[OSD([sQuery(id+"F0.wireOp",EDGE,"E15.top"),sQuery(id+"F0.wireOp",EDGE,"E15.left")])]});
            var Q7;
            Q7=makeQuery(id+"F2.opExtrude","SWEPT_EDGE",EDGE,{"disambiguationData":[OSD([sQuery(id+"F0.wireOp",EDGE,"E14.top"),sQuery(id+"F0.wireOp",EDGE,"E14.left")])]});
            var Q8;
            Q8=makeQuery(id+"F2.opExtrude","SWEPT_EDGE",EDGE,{"disambiguationData":[OSD([sQuery(id+"F0.wireOp",EDGE,"E16.top"),sQuery(id+"F0.wireOp",EDGE,"E16.left")])]});
            var Q9;
            Q9=makeQuery(id+"F2.opExtrude","SWEPT_EDGE",EDGE,{"disambiguationData":[OSD([sQuery(id+"F0.wireOp",EDGE,"E16.top"),sQuery(id+"F0.wireOp",EDGE,"E16.right")])]});
            var Q10;
            Q10=makeQuery(id+"F2.opExtrude","SWEPT_EDGE",EDGE,{"disambiguationData":[OSD([sQuery(id+"F0.wireOp",EDGE,"E15.top"),sQuery(id+"F0.wireOp",EDGE,"E15.right")])]});
            var Q11;
            Q11=makeQuery(id+"F2.opExtrude","SWEPT_EDGE",EDGE,{"disambiguationData":[OSD([sQuery(id+"F0.wireOp",EDGE,"E14.top"),sQuery(id+"F0.wireOp",EDGE,"E14.right")])]});
            fillet(context, id + "F21", {"entities" : qUnion([Q0, Q1, Q2, Q3, Q4, Q5, Q6, Q7, Q8, Q9, Q10, Q11]), "radius" : 2 * mm, "tangentPropagation" : true, "allowEdgeOverflow" : false});
        }
        {
            var Q0;
            Q0=makeQuery(id+"F1.opExtrude","SWEPT_EDGE",EDGE,{"disambiguationData":[OSD([sQuery(id+"F0.wireOp",EDGE,"E18.bottom"),sQuery(id+"F0.wireOp",EDGE,"E18.right")])]});
            var Q1;
            Q1=makeQuery(id+"F1.opExtrude","SWEPT_EDGE",EDGE,{"disambiguationData":[OSD([sQuery(id+"F0.wireOp",EDGE,"E18.top"),sQuery(id+"F0.wireOp",EDGE,"E18.right")])]});
            var Q2;
            Q2=makeQuery(id+"F1.opExtrude","SWEPT_EDGE",EDGE,{"disambiguationData":[OSD([sQuery(id+"F0.wireOp",EDGE,"E18.top"),sQuery(id+"F0.wireOp",EDGE,"E18.left")])]});
            var Q3;
            Q3=makeQuery(id+"F1.opExtrude","SWEPT_EDGE",EDGE,{"disambiguationData":[OSD([sQuery(id+"F0.wireOp",EDGE,"E18.bottom"),sQuery(id+"F0.wireOp",EDGE,"E18.left")])]});
            var Q4;
            Q4=makeQuery(id+"F1.opExtrude","SWEPT_EDGE",EDGE,{"disambiguationData":[OSD([sQuery(id+"F0.wireOp",EDGE,"E19.top"),sQuery(id+"F0.wireOp",EDGE,"E19.right")])]});
            var Q5;
            Q5=makeQuery(id+"F1.opExtrude","SWEPT_EDGE",EDGE,{"disambiguationData":[OSD([sQuery(id+"F0.wireOp",EDGE,"E19.bottom"),sQuery(id+"F0.wireOp",EDGE,"E19.right")])]});
            var Q6;
            Q6=makeQuery(id+"F1.opExtrude","SWEPT_EDGE",EDGE,{"disambiguationData":[OSD([sQuery(id+"F0.wireOp",EDGE,"E19.bottom"),sQuery(id+"F0.wireOp",EDGE,"E19.left")])]});
            var Q7;
            Q7=makeQuery(id+"F1.opExtrude","SWEPT_EDGE",EDGE,{"disambiguationData":[OSD([sQuery(id+"F0.wireOp",EDGE,"E19.top"),sQuery(id+"F0.wireOp",EDGE,"E19.left")])]});
            var Q8;
            Q8=makeQuery(id+"F1.opExtrude","SWEPT_EDGE",EDGE,{"disambiguationData":[OSD([sQuery(id+"F0.wireOp",EDGE,"E17.top"),sQuery(id+"F0.wireOp",EDGE,"E17.left")])]});
            var Q9;
            Q9=makeQuery(id+"F1.opExtrude","SWEPT_EDGE",EDGE,{"disambiguationData":[OSD([sQuery(id+"F0.wireOp",EDGE,"E17.top"),sQuery(id+"F0.wireOp",EDGE,"E17.right")])]});
            var Q10;
            Q10=makeQuery(id+"F1.opExtrude","SWEPT_EDGE",EDGE,{"disambiguationData":[OSD([sQuery(id+"F0.wireOp",EDGE,"E17.bottom"),sQuery(id+"F0.wireOp",EDGE,"E17.right")])]});
            var Q11;
            Q11=makeQuery(id+"F1.opExtrude","SWEPT_EDGE",EDGE,{"disambiguationData":[OSD([sQuery(id+"F0.wireOp",EDGE,"E17.bottom"),sQuery(id+"F0.wireOp",EDGE,"E17.left")])]});
            fillet(context, id + "F22", {"entities" : qUnion([Q0, Q1, Q2, Q3, Q4, Q5, Q6, Q7, Q8, Q9, Q10, Q11]), "radius" : 3 * mm, "tangentPropagation" : true, "allowEdgeOverflow" : false});
        }
        {
            var Q0;
            {var subQ0=sQuery(id+"F0.wireOp",EDGE,"E2");var subQ1=sQuery(id+"F0.wireOp",EDGE,"E0");Q0=makeQuery(id+"F16.boolean.opBoolean","MERGE",EDGE,{"derivedFrom":[makeQuery(id+"F14.boolean.opBoolean","INTERSECT",EDGE,{"derivedFrom":[makeQuery(id+"F7.boolean.opBoolean","MERGE",FACE,{"derivedFrom":[makeQuery(id+"F5.boolean.opBoolean","MERGE",FACE,{"derivedFrom":[makeQuery(id+"F1.opExtrude","SWEPT_FACE",FACE,{"disambiguationData":[OSD([subQ0]),TDD([makeQuery(id+"F0.imprint","IMPRINT",EDGE,{"disambiguationData":[TD([[makeQuery(id+"F0.imprint","INTERSECT",VERTEX,{"disambiguationData":[OD(1.0)],"derivedFrom":[subQ1,subQ0]}),-1.0]])],"derivedFrom":subQ0})])]}),makeQuery(id+"F3.boolean.opBoolean","MERGE",FACE,{"derivedFrom":[makeQuery(id+"F1.opExtrude","SWEPT_FACE",FACE,{"disambiguationData":[OSD([subQ0]),TDD([makeQuery(id+"F0.imprint","IMPRINT",EDGE,{"disambiguationData":[TD([[makeQuery(id+"F0.imprint","INTERSECT",VERTEX,{"derivedFrom":[subQ0,sQuery(id+"F0.wireOp",EDGE,"E21")]}),-1.0]])],"derivedFrom":subQ0})])]}),makeQuery(id+"F3.opExtrude","SWEPT_FACE",FACE,{"disambiguationData":[OSD([subQ0])]})]}),makeQuery(id+"F5.opExtrude","SWEPT_FACE",FACE,{"disambiguationData":[OSD([subQ0])]})]}),makeQuery(id+"F7.opExtrude","SWEPT_FACE",FACE,{"disambiguationData":[OSD([sQuery(id+"F6.wireOp",EDGE,"E31"),sQuery(id+"F6.wireOp",EDGE,"E32")])]})]}),makeQuery(id+"F14.opExtrude","CAP_FACE",FACE,{"disambiguationData":[OSD([sQuery(id+"F12.wireOp",EDGE,"E54"),sQuery(id+"F12.wireOp",EDGE,"E57"),sQuery(id+"F12.wireOp",EDGE,"E61"),sQuery(id+"F12.wireOp",EDGE,"E62"),sQuery(id+"F12.wireOp",EDGE,"E66"),sQuery(id+"F12.wireOp",EDGE,"E67"),sQuery(id+"F12.wireOp",EDGE,"E72"),sQuery(id+"F12.wireOp",EDGE,"E73")])],"isStart":true})]}),makeQuery(id+"F16.opExtrude","SWEPT_EDGE",EDGE,{"disambiguationData":[OSD([sQuery(id+"F15.wireOp",EDGE,"E90"),sQuery(id+"F15.wireOp",EDGE,"E91")])]})]});}
            var Q1;
            Q1=makeQuery(id+"F3.opExtrude","SWEPT_EDGE",EDGE,{"disambiguationData":[OSD([sQuery(id+"F0.wireOp",EDGE,"E2"),sQuery(id+"F0.wireOp",EDGE,"E6")])]});
            var Q2;
            Q2=makeQuery(id+"F1.opExtrude","SWEPT_EDGE",EDGE,{"disambiguationData":[OSD([sQuery(id+"F0.wireOp",EDGE,"E1"),sQuery(id+"F0.wireOp",EDGE,"E7")])]});
            var Q3;
            Q3=makeQuery(id+"F1.opExtrude","SWEPT_EDGE",EDGE,{"disambiguationData":[OSD([sQuery(id+"F0.wireOp",EDGE,"E1"),sQuery(id+"F0.wireOp",EDGE,"E10")])]});
            var Q4;
            Q4=makeQuery(id+"F16.boolean.opBoolean","MERGE",EDGE,{"derivedFrom":[makeQuery(id+"F14.boolean.opBoolean","INTERSECT",EDGE,{"derivedFrom":[makeQuery(id+"F7.boolean.opBoolean","MERGE",FACE,{"derivedFrom":[makeQuery(id+"F1.opExtrude","SWEPT_FACE",FACE,{"disambiguationData":[OSD([sQuery(id+"F0.wireOp",EDGE,"E12")])]}),makeQuery(id+"F7.opExtrude","SWEPT_FACE",FACE,{"disambiguationData":[OSD([sQuery(id+"F6.wireOp",EDGE,"E29"),sQuery(id+"F6.wireOp",EDGE,"E30")])]})]}),makeQuery(id+"F14.opExtrude","CAP_FACE",FACE,{"disambiguationData":[OSD([sQuery(id+"F12.wireOp",EDGE,"E54"),sQuery(id+"F12.wireOp",EDGE,"E57"),sQuery(id+"F12.wireOp",EDGE,"E61"),sQuery(id+"F12.wireOp",EDGE,"E62"),sQuery(id+"F12.wireOp",EDGE,"E66"),sQuery(id+"F12.wireOp",EDGE,"E67"),sQuery(id+"F12.wireOp",EDGE,"E72"),sQuery(id+"F12.wireOp",EDGE,"E73")])],"isStart":true})]}),makeQuery(id+"F16.opExtrude","SWEPT_EDGE",EDGE,{"disambiguationData":[OSD([sQuery(id+"F15.wireOp",EDGE,"E85"),sQuery(id+"F15.wireOp",EDGE,"E86")])]})]});
            fillet(context, id + "F23", {"entities" : qUnion([Q0, Q1, Q2, Q3, Q4]), "radius" : 7 * mm, "tangentPropagation" : true, "allowEdgeOverflow" : false});
        }
        {
            var Q0;
            {var subQ0=sQuery(id+"F6.wireOp",EDGE,"E43");var subQ1=sQuery(id+"F6.wireOp",EDGE,"E42");Q0=makeQuery(id+"F16.boolean.opBoolean","MERGE",EDGE,{"derivedFrom":[makeQuery(id+"F14.boolean.opBoolean","MERGE",EDGE,{"derivedFrom":[makeQuery(id+"F10.boolean.opBoolean","MERGE",EDGE,{"derivedFrom":[makeQuery(id+"F1.opExtrude","SWEPT_EDGE",EDGE,{"disambiguationData":[OSD([sQuery(id+"F0.wireOp",EDGE,"E4"),sQuery(id+"F0.wireOp",EDGE,"E5")])]}),makeQuery(id+"F10.opExtrude","SWEPT_EDGE",EDGE,{"disambiguationData":[OSD([subQ1,subQ0])]})]}),makeQuery(id+"F11.opExtrude","SWEPT_EDGE",EDGE,{"disambiguationData":[OSD([subQ1,subQ0])]}),makeQuery(id+"F14.opExtrude","CAP_EDGE",EDGE,{"disambiguationData":[OSD([sQuery(id+"F12.wireOp",EDGE,"E68")])],"isStart":false})]}),makeQuery(id+"F16.opExtrude","SWEPT_EDGE",EDGE,{"disambiguationData":[OSD([sQuery(id+"F15.wireOp",EDGE,"E88"),sQuery(id+"F15.wireOp",EDGE,"E89")])]})]});}
            var Q1;
            {var subQ0=sQuery(id+"F6.wireOp",EDGE,"E42");var subQ1=sQuery(id+"F6.wireOp",EDGE,"E41");Q1=makeQuery(id+"F16.boolean.opBoolean","MERGE",EDGE,{"derivedFrom":[makeQuery(id+"F14.boolean.opBoolean","MERGE",EDGE,{"derivedFrom":[makeQuery(id+"F10.boolean.opBoolean","MERGE",EDGE,{"derivedFrom":[makeQuery(id+"F1.opExtrude","SWEPT_EDGE",EDGE,{"disambiguationData":[OSD([sQuery(id+"F0.wireOp",EDGE,"E3"),sQuery(id+"F0.wireOp",EDGE,"E4")])]}),makeQuery(id+"F10.opExtrude","SWEPT_EDGE",EDGE,{"disambiguationData":[OSD([subQ1,subQ0])]})]}),makeQuery(id+"F11.opExtrude","SWEPT_EDGE",EDGE,{"disambiguationData":[OSD([subQ1,subQ0])]}),makeQuery(id+"F14.opExtrude","CAP_EDGE",EDGE,{"disambiguationData":[OSD([sQuery(id+"F12.wireOp",EDGE,"E68")])],"isStart":true})]}),makeQuery(id+"F16.opExtrude","SWEPT_EDGE",EDGE,{"disambiguationData":[OSD([sQuery(id+"F15.wireOp",EDGE,"E89"),sQuery(id+"F15.wireOp",EDGE,"E90")])]})]});}
            var Q2;
            Q2=makeQuery(id+"F16.boolean.opBoolean","MERGE",EDGE,{"derivedFrom":[makeQuery(id+"F7.boolean.opBoolean","MERGE",EDGE,{"derivedFrom":[makeQuery(id+"F1.opExtrude","SWEPT_EDGE",EDGE,{"disambiguationData":[OSD([sQuery(id+"F0.wireOp",EDGE,"E5"),sQuery(id+"F0.wireOp",EDGE,"E7")])]}),makeQuery(id+"F7.opExtrude","SWEPT_EDGE",EDGE,{"disambiguationData":[OSD([sQuery(id+"F6.wireOp",EDGE,"E39"),sQuery(id+"F6.wireOp",EDGE,"E40")])]})]}),makeQuery(id+"F16.opExtrude","SWEPT_EDGE",EDGE,{"disambiguationData":[OSD([sQuery(id+"F15.wireOp",EDGE,"E87"),sQuery(id+"F15.wireOp",EDGE,"E88")])]})]});
            var Q3;
            Q3=makeQuery(id+"F16.boolean.opBoolean","MERGE",EDGE,{"derivedFrom":[makeQuery(id+"F7.opExtrude","SWEPT_EDGE",EDGE,{"disambiguationData":[OSD([sQuery(id+"F0.wireOp",EDGE,"E7"),sQuery(id+"F6.wireOp",EDGE,"E38"),sQuery(id+"F6.wireOp",EDGE,"E39")])]}),makeQuery(id+"F16.opExtrude","SWEPT_EDGE",EDGE,{"disambiguationData":[OSD([sQuery(id+"F15.wireOp",EDGE,"E86"),sQuery(id+"F15.wireOp",EDGE,"E87")])]})]});
            var Q4;
            Q4=makeQuery(id+"F1.opExtrude","SWEPT_EDGE",EDGE,{"disambiguationData":[OSD([sQuery(id+"F0.wireOp",EDGE,"E6"),sQuery(id+"F0.wireOp",EDGE,"E8")])]});
            var Q5;
            Q5=makeQuery(id+"F1.opExtrude","SWEPT_EDGE",EDGE,{"disambiguationData":[OSD([sQuery(id+"F0.wireOp",EDGE,"E8"),sQuery(id+"F0.wireOp",EDGE,"E9")])]});
            var Q6;
            Q6=makeQuery(id+"F1.opExtrude","SWEPT_EDGE",EDGE,{"disambiguationData":[OSD([sQuery(id+"F0.wireOp",EDGE,"E9"),sQuery(id+"F0.wireOp",EDGE,"E10")])]});
            fillet(context, id + "F24", {"entities" : qUnion([Q0, Q1, Q2, Q3, Q4, Q5, Q6]), "radius" : 3 * mm, "tangentPropagation" : true, "allowEdgeOverflow" : false});
        }
        {
            var Q0;
            Q0=makeQuery(id+"F15.imprint","IMPRINT",FACE,{"disambiguationData":[TD([[makeQuery(id+"F15.imprint","IMPRINT",EDGE,{"derivedFrom":sQuery(id+"F15.wireOp",EDGE,"E97.bottom")}),-1.0]])]});
            extrude(context, id + "F25", {"entities" : qUnion([Q0]), "operationType" : NewBodyOperationType.ADD, "depth" : 5 * mm});
        }
        {
            var Q0;
            Q0=makeQuery(id+"F25.opExtrude","CAP_FACE",FACE,{"disambiguationData":[OSD([sQuery(id+"F15.wireOp",EDGE,"E97.bottom"),sQuery(id+"F15.wireOp",EDGE,"E97.top"),sQuery(id+"F15.wireOp",EDGE,"E97.left"),sQuery(id+"F15.wireOp",EDGE,"E97.right")])],"isStart":false});
            var sketch = newSketch(context, id + "F26", { "sketchPlane" : qUnion([Q0])});
            skText(sketch, "E98", { "text": "LUMEX", "fontName": "Arimo-Italic.ttf"});
            const initialGuessF26  = {"E98": [-0.00665, -0.03285, 1, 0, 0.00325]};
            skSetInitialGuess(sketch, initialGuessF26);
            skSolve(sketch);
        }
        {
            var Q0;
            Q0 = qSketchRegion(id + "F26", true);
            extrude(context, id + "F27", {"entities" : qUnion([Q0]), "operationType" : NewBodyOperationType.ADD, "depth" : 1 * mm});
        }
        {
            var Q0;
            {var subQ0=sQuery(id+"F12.wireOp",EDGE,"E75");var subQ1=sQuery(id+"F12.wireOp",EDGE,"E74");var subQ2=sQuery(id+"F12.wireOp",EDGE,"E67");var subQ3=sQuery(id+"F12.wireOp",EDGE,"E66");var subQ4=sQuery(id+"F12.wireOp",EDGE,"E60");var subQ5=sQuery(id+"F12.wireOp",EDGE,"E59");var subQ6=sQuery(id+"F12.wireOp",EDGE,"E57");var subQ7=sQuery(id+"F12.wireOp",EDGE,"E54");var subQ8=sQuery(id+"F12.wireOp",EDGE,"E73");var subQ9=sQuery(id+"F12.wireOp",EDGE,"E72");var subQ10=sQuery(id+"F12.wireOp",EDGE,"E62");var subQ11=sQuery(id+"F12.wireOp",EDGE,"E61");var subQ12=sQuery(id+"F6.wireOp",EDGE,"E43");var subQ13=sQuery(id+"F6.wireOp",EDGE,"E40");var subQ14=sQuery(id+"F0.wireOp",EDGE,"E5");Q0=makeQuery(id+"F16.boolean.opBoolean","MERGE",FACE,{"derivedFrom":[makeQuery(id+"F14.boolean.opBoolean","MERGE",FACE,{"derivedFrom":[makeQuery(id+"F13.boolean.opBoolean","MERGE",FACE,{"derivedFrom":[makeQuery(id+"F11.boolean.opBoolean","MERGE",FACE,{"derivedFrom":[makeQuery(id+"F10.boolean.opBoolean","MERGE",FACE,{"derivedFrom":[makeQuery(id+"F7.boolean.opBoolean","MERGE",FACE,{"derivedFrom":[makeQuery(id+"F1.opExtrude","SWEPT_FACE",FACE,{"disambiguationData":[OSD([subQ14])]}),makeQuery(id+"F7.opExtrude","SWEPT_FACE",FACE,{"disambiguationData":[OSD([subQ13])]}),makeQuery(id+"F7.opExtrude","SWEPT_FACE",FACE,{"disambiguationData":[OSD([subQ14])]})]}),makeQuery(id+"F10.opExtrude","SWEPT_FACE",FACE,{"disambiguationData":[OSD([subQ13])]}),makeQuery(id+"F10.opExtrude","SWEPT_FACE",FACE,{"disambiguationData":[OSD([subQ12])]})]}),makeQuery(id+"F11.opExtrude","SWEPT_FACE",FACE,{"disambiguationData":[OSD([subQ13])]}),makeQuery(id+"F11.opExtrude","SWEPT_FACE",FACE,{"disambiguationData":[OSD([subQ12])]})]}),makeQuery(id+"F13.opExtrude","CAP_FACE",FACE,{"disambiguationData":[OSD([sQuery(id+"F12.wireOp",EDGE,"E58.bottom"),sQuery(id+"F12.wireOp",EDGE,"E58.top"),subQ5,subQ4,subQ11,subQ10,sQuery(id+"F12.wireOp",EDGE,"E65")])],"isStart":false}),makeQuery(id+"F13.opExtrude","CAP_FACE",FACE,{"disambiguationData":[OSD([subQ3,subQ2,sQuery(id+"F12.wireOp",EDGE,"E69"),subQ9,subQ8,subQ1,subQ0])],"isStart":false})]}),makeQuery(id+"F14.opExtrude","CAP_FACE",FACE,{"disambiguationData":[OSD([subQ7,subQ6,subQ11,subQ10,subQ3,subQ2,subQ9,subQ8])],"isStart":false}),makeQuery(id+"F14.opExtrude","CAP_FACE",FACE,{"disambiguationData":[OSD([subQ7,sQuery(id+"F12.wireOp",EDGE,"E55"),subQ6,subQ5,subQ4])],"isStart":false}),makeQuery(id+"F14.opExtrude","CAP_FACE",FACE,{"disambiguationData":[OSD([subQ3,subQ2,sQuery(id+"F12.wireOp",EDGE,"E68"),subQ1,subQ0])],"isStart":false})]}),makeQuery(id+"F16.opExtrude","SWEPT_FACE",FACE,{"disambiguationData":[OSD([sQuery(id+"F15.wireOp",EDGE,"E88")])]})]});}
            var sketch = newSketch(context, id + "F28", { "sketchPlane" : qUnion([Q0])});
            skLineSegment(sketch, "E99", {"start": v(-29.8, 15.5) * mm, "end": v(-4.3, 15.5) * mm});
            skCircle(sketch, "E100", {"center": v(-4.3, 15.5) * mm, "radius": 1.6 * mm});
            skSolve(sketch);
        }
        {
            var Q0;
            Q0=sQuery(id+"F28.wireOp",VERTEX,"E99.end");
            var Q1;
            Q1=makeQuery(id+"F1.opExtrude","SWEPT_BODY",BODY,{"disambiguationData":[OSD([sQuery(id+"F0.wireOp",EDGE,"E0"),sQuery(id+"F0.wireOp",EDGE,"E1"),sQuery(id+"F0.wireOp",EDGE,"E2"),sQuery(id+"F0.wireOp",EDGE,"E3"),sQuery(id+"F0.wireOp",EDGE,"E4"),sQuery(id+"F0.wireOp",EDGE,"E5"),sQuery(id+"F0.wireOp",EDGE,"E6"),sQuery(id+"F0.wireOp",EDGE,"E7"),sQuery(id+"F0.wireOp",EDGE,"E8"),sQuery(id+"F0.wireOp",EDGE,"E9"),sQuery(id+"F0.wireOp",EDGE,"E10"),sQuery(id+"F0.wireOp",EDGE,"E11"),sQuery(id+"F0.wireOp",EDGE,"E12"),sQuery(id+"F0.wireOp",EDGE,"E13"),sQuery(id+"F0.wireOp",EDGE,"E17.bottom"),sQuery(id+"F0.wireOp",EDGE,"E17.top"),sQuery(id+"F0.wireOp",EDGE,"E17.left"),sQuery(id+"F0.wireOp",EDGE,"E17.right"),sQuery(id+"F0.wireOp",EDGE,"E18.bottom"),sQuery(id+"F0.wireOp",EDGE,"E18.top"),sQuery(id+"F0.wireOp",EDGE,"E18.left"),sQuery(id+"F0.wireOp",EDGE,"E18.right"),sQuery(id+"F0.wireOp",EDGE,"E19.bottom"),sQuery(id+"F0.wireOp",EDGE,"E19.top"),sQuery(id+"F0.wireOp",EDGE,"E19.left"),sQuery(id+"F0.wireOp",EDGE,"E19.right"),sQuery(id+"F0.wireOp",EDGE,"E20"),sQuery(id+"F0.wireOp",EDGE,"E21"),sQuery(id+"F0.wireOp",EDGE,"E25"),sQuery(id+"F0.wireOp",EDGE,"E26")])]});
            hole(context, id + "F29", {"style" : HoleStyle.SIMPLE, "endStyle" : HoleEndStyle.THROUGH, "holeDiameter" : 3.5 * mm, "startFromSketch" : true, "locations" : qUnion([Q0]), "scope" : qUnion([Q1]), "isTappedThrough" : true});
        }
        {
            var Q0;
            Q0=makeQuery(id+"F25.opExtrude","CAP_FACE",FACE,{"disambiguationData":[OSD([sQuery(id+"F15.wireOp",EDGE,"E97.bottom"),sQuery(id+"F15.wireOp",EDGE,"E97.top"),sQuery(id+"F15.wireOp",EDGE,"E97.left"),sQuery(id+"F15.wireOp",EDGE,"E97.right")])],"isStart":false});
            var sketch = newSketch(context, id + "F30", { "sketchPlane" : qUnion([Q0])});
            skLineSegment(sketch, "E101.bottom", {"start": v(-7.15, -27) * mm, "end": v(9.6, -27) * mm});
            skLineSegment(sketch, "E101.top", {"start": v(-7.15, -34.85) * mm, "end": v(9.6, -34.85) * mm});
            skLineSegment(sketch, "E101.left", {"start": v(-7.15, -27) * mm, "end": v(-7.15, -34.85) * mm});
            skLineSegment(sketch, "E101.right", {"start": v(9.6, -27) * mm, "end": v(9.6, -34.85) * mm});
            skSolve(sketch);
        }
        {
            var Q0;
            Q0=makeQuery(id+"F30.imprint","IMPRINT",FACE,{"disambiguationData":[TD([[makeQuery(id+"F30.imprint","IMPRINT",EDGE,{"derivedFrom":sQuery(id+"F30.wireOp",EDGE,"E101.bottom")}),1.0]])]});
            extrude(context, id + "F31", {"entities" : qUnion([Q0]), "operationType" : NewBodyOperationType.ADD, "depth" : 1.5 * mm});
        }
    });
